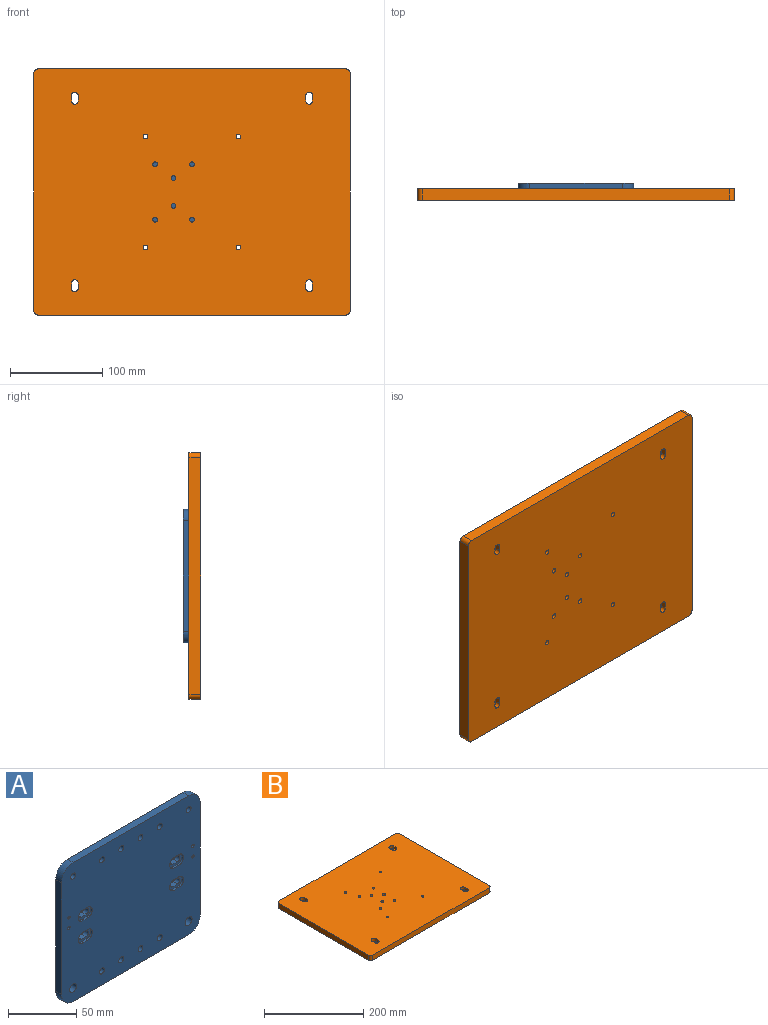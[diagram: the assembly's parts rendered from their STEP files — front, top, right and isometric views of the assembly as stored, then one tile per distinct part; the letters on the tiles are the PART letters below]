
ASSEMBLY  parts=2 mates=1
PART A: 62 faces, bbox 144.4x6x125 mm
  f0: plane 144.4x125mm, normal (0,1,0), area 17433.2mm2, adj f2,f3,f4,f5,f6,f7,f8,f9
  f1: plane 144.4x125mm, normal (0,-1,0), area 17143.4mm2, adj f2,f3,f4,f5,f6,f7,f8,f9
  f2: plane 120x6mm, normal (0,0,-1), area 720mm2, adj f0,f1,f3,f13
  f3: cylinder r=12.2mm len=12.2mm, axis (0,1,0), area 115mm2, adj f0,f1,f2,f4
  f4: plane 100.6x6mm, normal (1,0,0), area 603.6mm2, adj f0,f1,f3,f5
  f5: cylinder r=12.2mm len=12.2mm, axis (0,1,0), area 115mm2, adj f0,f1,f4,f6
  f6: plane 120x6mm, normal (0,0,1), area 720mm2, adj f0,f1,f5,f7
  f7: cylinder r=12.2mm len=12.2mm, axis (0,1,0), area 115mm2, adj f0,f1,f6,f8
  f8: plane 100.6x6mm, normal (-1,0,0), area 603.6mm2, adj f0,f1,f7,f13
  f9: cylinder r=2.55mm len=6mm, axis (0,1,0), area 96.1mm2, adj f0,f1
  f10: cylinder r=2.55mm len=6mm, axis (0,1,0), area 96.1mm2, adj f0,f1
  f11: cylinder r=3.6mm len=7.2mm, axis (0,1,0), area 135.7mm2, adj f0,f1
  f12: cylinder r=3.6mm len=7.2mm, axis (0,1,0), area 135.7mm2, adj f0,f1
  f13: cylinder r=12.2mm len=12.2mm, axis (0,1,0), area 115mm2, adj f0,f1,f2,f8
  f14: cylinder r=2.55mm len=6mm, axis (0,-1,0), area 96.1mm2, adj f0,f1
  f15: cylinder r=2.55mm len=6mm, axis (0,-1,0), area 96.1mm2, adj f0,f1
  f16: cylinder r=2.55mm len=6mm, axis (0,-1,0), area 96.1mm2, adj f0,f1
  f17: cylinder r=2.55mm len=6mm, axis (0,-1,0), area 96.1mm2, adj f0,f1
  f18: cylinder r=2.55mm len=6mm, axis (0,-1,0), area 96.1mm2, adj f0,f1
  f19: cylinder r=2.55mm len=6mm, axis (0,-1,0), area 96.1mm2, adj f0,f1
  f20: cylinder r=2.55mm len=6mm, axis (0,-1,0), area 96.1mm2, adj f0,f1
  f21: cylinder r=2.55mm len=6mm, axis (0,-1,0), area 96.1mm2, adj f0,f1
  f22: plane 5x1.6mm, normal (0,0,-1), area 8mm2, adj f1,f23,f25,f26
  f23: cylinder r=4.75mm len=9.5mm, axis (0,-1,0), area 23.9mm2, adj f1,f22,f24,f26
  f24: plane 5x1.6mm, normal (0,0,1), area 8mm2, adj f1,f23,f25,f26
  f25: cylinder r=4.75mm len=9.5mm, axis (0,-1,0), area 23.9mm2, adj f1,f22,f24,f26
  f26: plane 14.5x9.5mm, normal (0,-1,0), area 72.5mm2, adj f22,f23,f24,f25,f36,f37,f38,f39
  f27: plane 5x1.6mm, normal (0,0,-1), area 8mm2, adj f1,f28,f30,f31
  f28: cylinder r=4.75mm len=9.5mm, axis (0,-1,0), area 23.9mm2, adj f1,f27,f29,f31
  f29: plane 5x1.6mm, normal (0,0,1), area 8mm2, adj f1,f28,f30,f31
  f30: cylinder r=4.75mm len=9.5mm, axis (0,-1,0), area 23.9mm2, adj f1,f27,f29,f31
  f31: plane 14.5x9.5mm, normal (0,-1,0), area 72.5mm2, adj f27,f28,f29,f30,f32,f33,f34,f35
  f32: cylinder r=2.55mm len=5.1mm, axis (0,-1,0), area 35.2mm2, adj f0,f31,f33,f35
  f33: plane 5x4.4mm, normal (0,0,1), area 22mm2, adj f0,f31,f32,f34
  f34: cylinder r=2.55mm len=5.1mm, axis (0,-1,0), area 35.2mm2, adj f0,f31,f33,f35
  f35: plane 5x4.4mm, normal (0,0,-1), area 22mm2, adj f0,f31,f32,f34
  f36: cylinder r=2.55mm len=5.1mm, axis (0,-1,0), area 35.2mm2, adj f0,f26,f37,f39
  f37: plane 5x4.4mm, normal (0,0,1), area 22mm2, adj f0,f26,f36,f38
  f38: cylinder r=2.55mm len=5.1mm, axis (0,-1,0), area 35.2mm2, adj f0,f26,f37,f39
  f39: plane 5x4.4mm, normal (0,0,-1), area 22mm2, adj f0,f26,f36,f38
  f40: cylinder r=1.25mm len=6mm, axis (0,-1,0), area 47.1mm2, adj f0,f1
  f41: cylinder r=1.25mm len=6mm, axis (0,-1,0), area 47.1mm2, adj f0,f1
  f42: plane 5x1.6mm, normal (0,0,-1), area 8mm2, adj f1,f43,f45,f46
  f43: cylinder r=4.75mm len=9.5mm, axis (0,-1,0), area 23.9mm2, adj f1,f42,f44,f46
  f44: plane 5x1.6mm, normal (0,0,1), area 8mm2, adj f1,f43,f45,f46
  f45: cylinder r=4.75mm len=9.5mm, axis (0,-1,0), area 23.9mm2, adj f1,f42,f44,f46
  f46: plane 14.5x9.5mm, normal (0,-1,0), area 72.5mm2, adj f42,f43,f44,f45,f56,f57,f58,f59
  f47: plane 5x1.6mm, normal (0,0,-1), area 8mm2, adj f1,f48,f50,f51
  f48: cylinder r=4.75mm len=9.5mm, axis (0,-1,0), area 23.9mm2, adj f1,f47,f49,f51
  f49: plane 5x1.6mm, normal (0,0,1), area 8mm2, adj f1,f48,f50,f51
  f50: cylinder r=4.75mm len=9.5mm, axis (0,-1,0), area 23.9mm2, adj f1,f47,f49,f51
  f51: plane 14.5x9.5mm, normal (0,-1,0), area 72.5mm2, adj f47,f48,f49,f50,f52,f53,f54,f55
  f52: plane 5x4.4mm, normal (0,0,1), area 22mm2, adj f0,f51,f53,f55
  f53: cylinder r=2.55mm len=5.1mm, axis (0,-1,0), area 35.2mm2, adj f0,f51,f52,f54
  f54: plane 5x4.4mm, normal (0,0,-1), area 22mm2, adj f0,f51,f53,f55
  f55: cylinder r=2.55mm len=5.1mm, axis (0,-1,0), area 35.2mm2, adj f0,f51,f52,f54
  f56: plane 5x4.4mm, normal (0,0,1), area 22mm2, adj f0,f46,f57,f59
  f57: cylinder r=2.55mm len=5.1mm, axis (0,-1,0), area 35.2mm2, adj f0,f46,f56,f58
  f58: plane 5x4.4mm, normal (0,0,-1), area 22mm2, adj f0,f46,f57,f59
  f59: cylinder r=2.55mm len=5.1mm, axis (0,-1,0), area 35.2mm2, adj f0,f46,f56,f58
  f60: cylinder r=1.25mm len=6mm, axis (0,-1,0), area 47.1mm2, adj f0,f1
  f61: cylinder r=1.25mm len=6mm, axis (0,-1,0), area 47.1mm2, adj f0,f1
PART B: 58 faces, bbox 342.9x266.7x12.7 mm
  f0: plane 6x5.7mm, normal (1,0,0), area 34.2mm2, adj f1,f3,f21,f41
  f1: cylinder r=3.57mm len=7.14mm, axis (0,0,1), area 63.9mm2, adj f0,f2,f21,f41
  f2: plane 6x5.7mm, normal (-1,0,0), area 34.2mm2, adj f1,f3,f21,f41
  f3: cylinder r=3.57mm len=7.14mm, axis (0,0,1), area 63.9mm2, adj f0,f2,f21,f41
  f4: plane 6x5.7mm, normal (-1,0,0), area 34.2mm2, adj f5,f7,f21,f36
  f5: cylinder r=3.57mm len=7.14mm, axis (0,0,1), area 63.9mm2, adj f4,f6,f21,f36
  f6: plane 6x5.7mm, normal (1,0,0), area 34.2mm2, adj f5,f7,f21,f36
  f7: cylinder r=3.57mm len=7.14mm, axis (0,0,1), area 63.9mm2, adj f4,f6,f21,f36
  f8: plane 6x5.7mm, normal (-1,0,0), area 34.2mm2, adj f9,f11,f21,f31
  f9: cylinder r=3.57mm len=7.14mm, axis (0,0,1), area 63.9mm2, adj f8,f10,f21,f31
  f10: plane 6x5.7mm, normal (1,0,0), area 34.2mm2, adj f9,f11,f21,f31
  f11: cylinder r=3.57mm len=7.14mm, axis (0,0,1), area 63.9mm2, adj f8,f10,f21,f31
  f12: plane 6x5.7mm, normal (1,0,0), area 34.2mm2, adj f13,f15,f21,f26
  f13: cylinder r=3.57mm len=7.14mm, axis (0,0,1), area 63.9mm2, adj f12,f14,f21,f26
  f14: plane 6x5.7mm, normal (-1,0,0), area 34.2mm2, adj f13,f15,f21,f26
  f15: cylinder r=3.57mm len=7.14mm, axis (0,0,1), area 63.9mm2, adj f12,f14,f21,f26
  f16: plane 332.9x12.7mm, normal (0,-1,0), area 4227.8mm2, adj f20,f21,f42,f45
  f17: plane 256.7x12.7mm, normal (1,0,0), area 3260.1mm2, adj f20,f21,f42,f43
  f18: plane 332.9x12.7mm, normal (0,1,0), area 4227.8mm2, adj f20,f21,f43,f44
  f19: plane 256.7x12.7mm, normal (-1,0,0), area 3260.1mm2, adj f20,f21,f44,f45
  f20: plane 342.9x266.7mm, normal (0,0,1), area 90453.6mm2, adj f16,f17,f18,f19,f22,f23,f24,f25
  f21: plane 342.9x266.7mm, normal (0,0,-1), area 90894.4mm2, adj f0,f1,f2,f3,f4,f5,f6,f7
  f22: plane 7x6mm, normal (1,0,0), area 42mm2, adj f20,f23,f25,f26
  f23: cylinder r=6mm len=12mm, axis (0,0,1), area 131.9mm2, adj f20,f22,f24,f26
  f24: plane 7x6mm, normal (-1,0,0), area 42mm2, adj f20,f23,f25,f26
  f25: cylinder r=6mm len=12mm, axis (0,0,1), area 131.9mm2, adj f20,f22,f24,f26
  f26: plane 18x12mm, normal (0,0,1), area 102.3mm2, adj f12,f13,f14,f15,f22,f23,f24,f25
  f27: plane 7x6mm, normal (-1,0,0), area 42mm2, adj f20,f28,f30,f31
  f28: cylinder r=6mm len=12mm, axis (0,0,1), area 131.9mm2, adj f20,f27,f29,f31
  f29: plane 7x6mm, normal (1,0,0), area 42mm2, adj f20,f28,f30,f31
  f30: cylinder r=6mm len=12mm, axis (0,0,1), area 131.9mm2, adj f20,f27,f29,f31
  f31: plane 18x12mm, normal (0,0,1), area 102.3mm2, adj f8,f9,f10,f11,f27,f28,f29,f30
  f32: plane 7x6mm, normal (-1,0,0), area 42mm2, adj f20,f33,f35,f36
  f33: cylinder r=6mm len=12mm, axis (0,0,1), area 131.9mm2, adj f20,f32,f34,f36
  f34: plane 7x6mm, normal (1,0,0), area 42mm2, adj f20,f33,f35,f36
  f35: cylinder r=6mm len=12mm, axis (0,0,1), area 131.9mm2, adj f20,f32,f34,f36
  f36: plane 18x12mm, normal (0,0,1), area 102.3mm2, adj f4,f5,f6,f7,f32,f33,f34,f35
  f37: plane 7x6mm, normal (1,0,0), area 42mm2, adj f20,f38,f40,f41
  f38: cylinder r=6mm len=12mm, axis (0,0,1), area 131.9mm2, adj f20,f37,f39,f41
  f39: plane 7x6mm, normal (-1,0,0), area 42mm2, adj f20,f38,f40,f41
  f40: cylinder r=6mm len=12mm, axis (0,0,1), area 131.9mm2, adj f20,f37,f39,f41
  f41: plane 18x12mm, normal (0,0,1), area 102.3mm2, adj f0,f1,f2,f3,f37,f38,f39,f40
  f42: cylinder r=5mm len=12.7mm, axis (0,0,1), area 99.7mm2, adj f16,f17,f20,f21
  f43: cylinder r=5mm len=12.7mm, axis (0,0,-1), area 99.7mm2, adj f17,f18,f20,f21
  f44: cylinder r=5mm len=12.7mm, axis (0,0,1), area 99.7mm2, adj f18,f19,f20,f21
  f45: cylinder r=5mm len=12.7mm, axis (0,0,-1), area 99.7mm2, adj f16,f19,f20,f21
  f46: cylinder r=3.17mm len=8mm, axis (0,0,1), area 159.6mm2, adj f20,f47
  f47: plane 6.35x6.35mm, normal (0,0,1), area 31.7mm2, adj f46
  f48: cylinder r=2.55mm len=12.7mm, axis (0,0,1), area 203.5mm2, adj f20,f21
  f49: cylinder r=2.55mm len=12.7mm, axis (0,0,1), area 203.5mm2, adj f20,f21
  f50: cylinder r=2.55mm len=12.7mm, axis (0,0,1), area 203.5mm2, adj f20,f21
  f51: cylinder r=2.55mm len=12.7mm, axis (0,0,1), area 203.5mm2, adj f20,f21
  f52: cylinder r=2.55mm len=12.7mm, axis (0,0,1), area 203.5mm2, adj f20,f21
  f53: cylinder r=2.55mm len=12.7mm, axis (0,0,1), area 203.5mm2, adj f20,f21
  f54: cylinder r=2.55mm len=12.7mm, axis (0,0,1), area 203.5mm2, adj f20,f21
  f55: cylinder r=2.55mm len=12.7mm, axis (0,0,1), area 203.5mm2, adj f20,f21
  f56: cylinder r=2.55mm len=12.7mm, axis (0,0,1), area 203.5mm2, adj f20,f21
  f57: cylinder r=2.55mm len=12.7mm, axis (0,0,1), area 203.5mm2, adj f20,f21
PLACE A rot(axis=(0,1,0),90deg) t=(-0.08,0,121.15)mm
PLACE B rot(axis=(-1,0,0),90deg) t=(0,-18.7,121.15)mm
MATE planar A.f1 <-> B.f20  axis (0,-1,0) through (0.03,-6,121.15)mm
